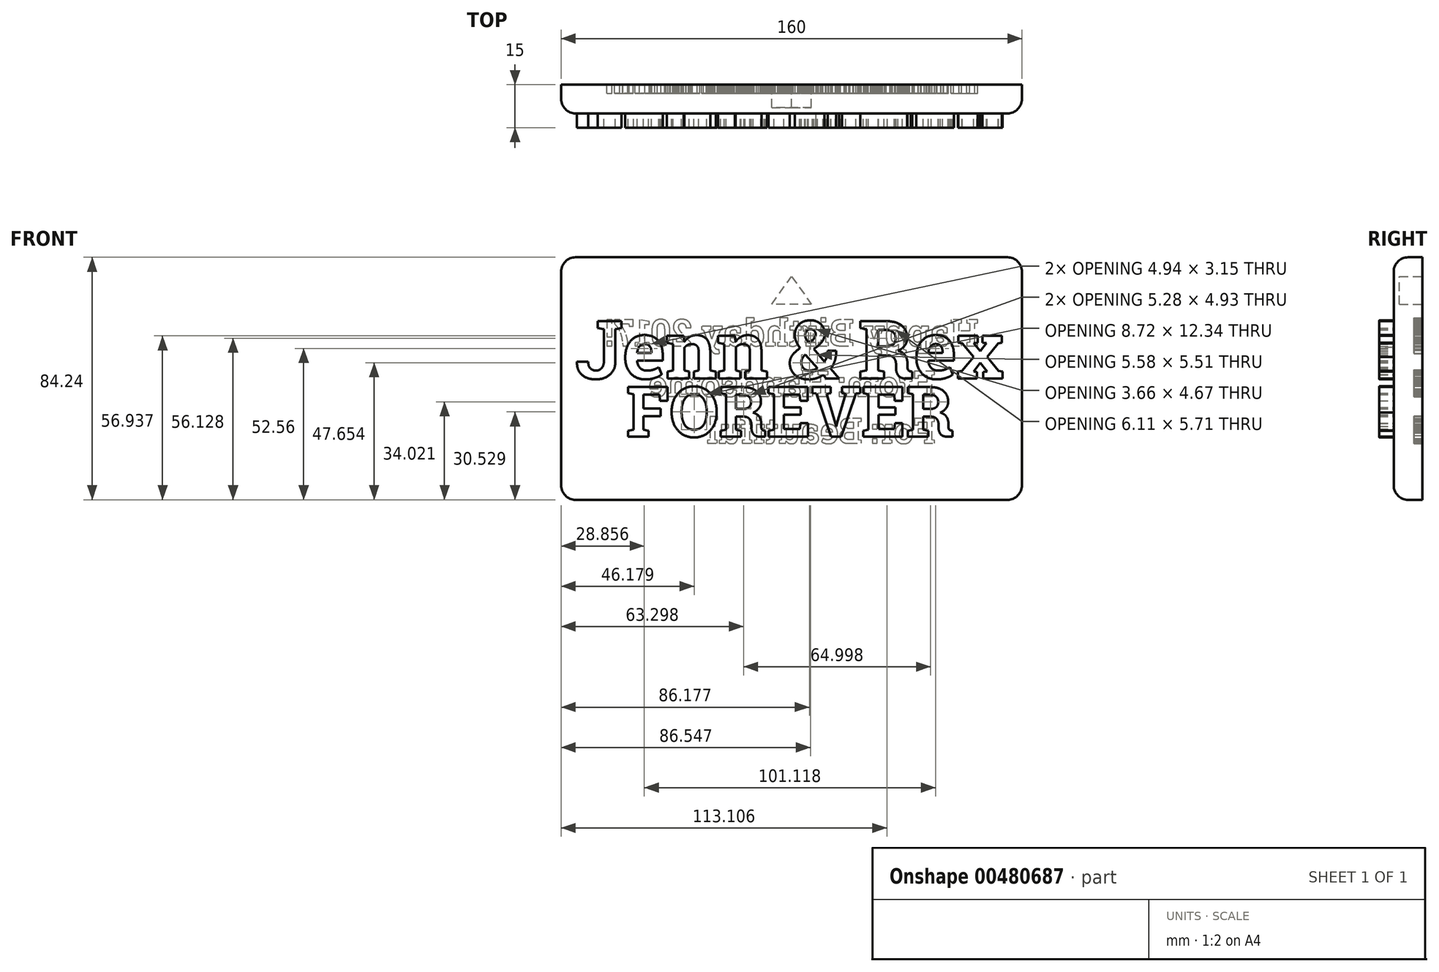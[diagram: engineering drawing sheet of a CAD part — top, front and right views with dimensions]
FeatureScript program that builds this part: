
annotation { "Feature Type Name" : "Feature", "Feature Type Description" : "" }
export const myFeature = defineFeature(function(context is Context, id is Id, definition is map)
    precondition{}
    {
        {
            var Q0;
            Q0=qCreatedBy(makeId("Front.planeOp"),FACE);
            var sketch = newSketch(context, id + "F0", { "sketchPlane" : qUnion([Q0])});
            skLineSegment(sketch, "E0.bottom", {"start": v(-80, 42.12) * mm, "end": v(80, 42.12) * mm});
            skLineSegment(sketch, "E0.top", {"start": v(-80, -42.12) * mm, "end": v(80, -42.12) * mm});
            skLineSegment(sketch, "E0.left", {"start": v(-80, 42.12) * mm, "end": v(-80, -42.12) * mm});
            skLineSegment(sketch, "E0.right", {"start": v(80, 42.12) * mm, "end": v(80, -42.12) * mm});
            skText(sketch, "E1", { "text": "Jenn & Rex", "fontName": "RobotoSlab-Bold.ttf"});
            skText(sketch, "E2", { "text": "FOREVER", "fontName": "RobotoSlab-Bold.ttf"});
            const initialGuessF0  = {"E1": [-0.075, 0, 1, 0, 0.0202], "E2": [-0.0574, -0.0202, 1, 0, 0.01745]};
            skSetInitialGuess(sketch, initialGuessF0);
            skSolve(sketch);
        }
        {
            var Q0;
            Q0=makeQuery(id+"F0.imprint","IMPRINT",FACE,{"disambiguationData":[TD([[makeQuery(id+"F0.imprint","IMPRINT",EDGE,{"derivedFrom":sQuery(id+"F0.wireOp",EDGE,"E1.sketch_text.stroke-0")}),-1.0]])]});
            var Q1;
            Q1=makeQuery(id+"F0.imprint","IMPRINT",FACE,{"disambiguationData":[TD([[makeQuery(id+"F0.imprint","IMPRINT",EDGE,{"derivedFrom":sQuery(id+"F0.wireOp",EDGE,"E1.sketch_text.stroke-18")}),-1.0]])]});
            var Q2;
            Q2=makeQuery(id+"F0.imprint","IMPRINT",FACE,{"disambiguationData":[TD([[makeQuery(id+"F0.imprint","IMPRINT",EDGE,{"derivedFrom":sQuery(id+"F0.wireOp",EDGE,"E1.sketch_text.stroke-42")}),-1.0]])]});
            var Q3;
            Q3=makeQuery(id+"F0.imprint","IMPRINT",FACE,{"disambiguationData":[TD([[makeQuery(id+"F0.imprint","IMPRINT",EDGE,{"derivedFrom":sQuery(id+"F0.wireOp",EDGE,"E1.sketch_text.stroke-68")}),-1.0]])]});
            var Q4;
            Q4=makeQuery(id+"F0.imprint","IMPRINT",FACE,{"disambiguationData":[TD([[makeQuery(id+"F0.imprint","IMPRINT",EDGE,{"derivedFrom":sQuery(id+"F0.wireOp",EDGE,"E1.sketch_text.stroke-94")}),-1.0]])]});
            var Q5;
            Q5=makeQuery(id+"F0.imprint","IMPRINT",FACE,{"disambiguationData":[TD([[makeQuery(id+"F0.imprint","IMPRINT",EDGE,{"derivedFrom":sQuery(id+"F0.wireOp",EDGE,"E1.sketch_text.stroke-136")}),-1.0]])]});
            var Q6;
            Q6=makeQuery(id+"F0.imprint","IMPRINT",FACE,{"disambiguationData":[TD([[makeQuery(id+"F0.imprint","IMPRINT",EDGE,{"derivedFrom":sQuery(id+"F0.wireOp",EDGE,"E2.sketch_text.stroke-95")}),-1.0]])]});
            var Q7;
            Q7=makeQuery(id+"F0.imprint","IMPRINT",FACE,{"disambiguationData":[TD([[makeQuery(id+"F0.imprint","IMPRINT",EDGE,{"derivedFrom":sQuery(id+"F0.wireOp",EDGE,"E2.sketch_text.stroke-74")}),-1.0]])]});
            var Q8;
            Q8=makeQuery(id+"F0.imprint","IMPRINT",FACE,{"disambiguationData":[TD([[makeQuery(id+"F0.imprint","IMPRINT",EDGE,{"derivedFrom":sQuery(id+"F0.wireOp",EDGE,"E2.sketch_text.stroke-38")}),-1.0]])]});
            var Q9;
            Q9=makeQuery(id+"F0.imprint","IMPRINT",FACE,{"disambiguationData":[TD([[makeQuery(id+"F0.imprint","IMPRINT",EDGE,{"derivedFrom":sQuery(id+"F0.wireOp",EDGE,"E2.sketch_text.stroke-18")}),-1.0]])]});
            var Q10;
            Q10=makeQuery(id+"F0.imprint","IMPRINT",FACE,{"disambiguationData":[TD([[makeQuery(id+"F0.imprint","IMPRINT",EDGE,{"derivedFrom":sQuery(id+"F0.wireOp",EDGE,"E2.sketch_text.stroke-0")}),-1.0]])]});
            var Q11;
            Q11=makeQuery(id+"F0.imprint","IMPRINT",FACE,{"disambiguationData":[TD([[makeQuery(id+"F0.imprint","IMPRINT",EDGE,{"derivedFrom":sQuery(id+"F0.wireOp",EDGE,"E1.sketch_text.stroke-172")}),-1.0]])]});
            var Q12;
            Q12=makeQuery(id+"F0.imprint","IMPRINT",FACE,{"disambiguationData":[TD([[makeQuery(id+"F0.imprint","IMPRINT",EDGE,{"derivedFrom":sQuery(id+"F0.wireOp",EDGE,"E1.sketch_text.stroke-196")}),-1.0]])]});
            var Q13;
            Q13=makeQuery(id+"F0.imprint","IMPRINT",FACE,{"disambiguationData":[TD([[makeQuery(id+"F0.imprint","IMPRINT",EDGE,{"derivedFrom":sQuery(id+"F0.wireOp",EDGE,"E2.sketch_text.stroke-134")}),-1.0]])]});
            var Q14;
            Q14=makeQuery(id+"F0.imprint","IMPRINT",FACE,{"disambiguationData":[TD([[makeQuery(id+"F0.imprint","IMPRINT",EDGE,{"derivedFrom":sQuery(id+"F0.wireOp",EDGE,"E2.sketch_text.stroke-113")}),-1.0]])]});
            extrude(context, id + "F1", {"entities" : qUnion([Q0, Q1, Q2, Q3, Q4, Q5, Q6, Q7, Q8, Q9, Q10, Q11, Q12, Q13, Q14]), "depth" : 5 * mm});
        }
        {
            var Q0;
            Q0=makeQuery(id+"F0.imprint","IMPRINT",FACE,{"disambiguationData":[TD([[makeQuery(id+"F0.imprint","IMPRINT",EDGE,{"derivedFrom":sQuery(id+"F0.wireOp",EDGE,"E0.bottom")}),-1.0]])]});
            var Q1;
            Q1=makeQuery(id+"F0.imprint","IMPRINT",FACE,{"disambiguationData":[TD([[makeQuery(id+"F0.imprint","IMPRINT",EDGE,{"derivedFrom":sQuery(id+"F0.wireOp",EDGE,"E1.sketch_text.stroke-165")}),1.0]])]});
            var Q2;
            Q2=makeQuery(id+"F0.imprint","IMPRINT",FACE,{"disambiguationData":[TD([[makeQuery(id+"F0.imprint","IMPRINT",EDGE,{"derivedFrom":sQuery(id+"F0.wireOp",EDGE,"E1.sketch_text.stroke-189")}),1.0]])]});
            var Q3;
            Q3=makeQuery(id+"F0.imprint","IMPRINT",FACE,{"disambiguationData":[TD([[makeQuery(id+"F0.imprint","IMPRINT",EDGE,{"derivedFrom":sQuery(id+"F0.wireOp",EDGE,"E1.sketch_text.stroke-119")}),1.0]])]});
            var Q4;
            Q4=makeQuery(id+"F0.imprint","IMPRINT",FACE,{"disambiguationData":[TD([[makeQuery(id+"F0.imprint","IMPRINT",EDGE,{"derivedFrom":sQuery(id+"F0.wireOp",EDGE,"E1.sketch_text.stroke-127")}),1.0]])]});
            var Q5;
            Q5=makeQuery(id+"F0.imprint","IMPRINT",FACE,{"disambiguationData":[TD([[makeQuery(id+"F0.imprint","IMPRINT",EDGE,{"derivedFrom":sQuery(id+"F0.wireOp",EDGE,"E2.sketch_text.stroke-163")}),1.0]])]});
            var Q6;
            Q6=makeQuery(id+"F0.imprint","IMPRINT",FACE,{"disambiguationData":[TD([[makeQuery(id+"F0.imprint","IMPRINT",EDGE,{"derivedFrom":sQuery(id+"F0.wireOp",EDGE,"E2.sketch_text.stroke-67")}),1.0]])]});
            var Q7;
            Q7=makeQuery(id+"F0.imprint","IMPRINT",FACE,{"disambiguationData":[TD([[makeQuery(id+"F0.imprint","IMPRINT",EDGE,{"derivedFrom":sQuery(id+"F0.wireOp",EDGE,"E2.sketch_text.stroke-28")}),1.0]])]});
            var Q8;
            Q8=makeQuery(id+"F0.imprint","IMPRINT",FACE,{"disambiguationData":[TD([[makeQuery(id+"F0.imprint","IMPRINT",EDGE,{"derivedFrom":sQuery(id+"F0.wireOp",EDGE,"E1.sketch_text.stroke-35")}),1.0]])]});
            var Q9;
            Q9=makeQuery(id+"F0.imprint","IMPRINT",FACE,{"disambiguationData":[TD([[makeQuery(id+"F0.imprint","IMPRINT",EDGE,{"derivedFrom":sQuery(id+"F0.wireOp",EDGE,"E1.sketch_text.stroke-18")}),-1.0]])]});
            var Q10;
            Q10=makeQuery(id+"F0.imprint","IMPRINT",FACE,{"disambiguationData":[TD([[makeQuery(id+"F0.imprint","IMPRINT",EDGE,{"derivedFrom":sQuery(id+"F0.wireOp",EDGE,"E1.sketch_text.stroke-0")}),-1.0]])]});
            var Q11;
            Q11=makeQuery(id+"F0.imprint","IMPRINT",FACE,{"disambiguationData":[TD([[makeQuery(id+"F0.imprint","IMPRINT",EDGE,{"derivedFrom":sQuery(id+"F0.wireOp",EDGE,"E1.sketch_text.stroke-42")}),-1.0]])]});
            var Q12;
            Q12=makeQuery(id+"F0.imprint","IMPRINT",FACE,{"disambiguationData":[TD([[makeQuery(id+"F0.imprint","IMPRINT",EDGE,{"derivedFrom":sQuery(id+"F0.wireOp",EDGE,"E1.sketch_text.stroke-68")}),-1.0]])]});
            var Q13;
            Q13=makeQuery(id+"F0.imprint","IMPRINT",FACE,{"disambiguationData":[TD([[makeQuery(id+"F0.imprint","IMPRINT",EDGE,{"derivedFrom":sQuery(id+"F0.wireOp",EDGE,"E1.sketch_text.stroke-94")}),-1.0]])]});
            var Q14;
            Q14=makeQuery(id+"F0.imprint","IMPRINT",FACE,{"disambiguationData":[TD([[makeQuery(id+"F0.imprint","IMPRINT",EDGE,{"derivedFrom":sQuery(id+"F0.wireOp",EDGE,"E1.sketch_text.stroke-136")}),-1.0]])]});
            var Q15;
            Q15=makeQuery(id+"F0.imprint","IMPRINT",FACE,{"disambiguationData":[TD([[makeQuery(id+"F0.imprint","IMPRINT",EDGE,{"derivedFrom":sQuery(id+"F0.wireOp",EDGE,"E1.sketch_text.stroke-172")}),-1.0]])]});
            var Q16;
            Q16=makeQuery(id+"F0.imprint","IMPRINT",FACE,{"disambiguationData":[TD([[makeQuery(id+"F0.imprint","IMPRINT",EDGE,{"derivedFrom":sQuery(id+"F0.wireOp",EDGE,"E1.sketch_text.stroke-196")}),-1.0]])]});
            var Q17;
            Q17=makeQuery(id+"F0.imprint","IMPRINT",FACE,{"disambiguationData":[TD([[makeQuery(id+"F0.imprint","IMPRINT",EDGE,{"derivedFrom":sQuery(id+"F0.wireOp",EDGE,"E2.sketch_text.stroke-134")}),-1.0]])]});
            var Q18;
            Q18=makeQuery(id+"F0.imprint","IMPRINT",FACE,{"disambiguationData":[TD([[makeQuery(id+"F0.imprint","IMPRINT",EDGE,{"derivedFrom":sQuery(id+"F0.wireOp",EDGE,"E2.sketch_text.stroke-113")}),-1.0]])]});
            var Q19;
            Q19=makeQuery(id+"F0.imprint","IMPRINT",FACE,{"disambiguationData":[TD([[makeQuery(id+"F0.imprint","IMPRINT",EDGE,{"derivedFrom":sQuery(id+"F0.wireOp",EDGE,"E2.sketch_text.stroke-95")}),-1.0]])]});
            var Q20;
            Q20=makeQuery(id+"F0.imprint","IMPRINT",FACE,{"disambiguationData":[TD([[makeQuery(id+"F0.imprint","IMPRINT",EDGE,{"derivedFrom":sQuery(id+"F0.wireOp",EDGE,"E2.sketch_text.stroke-74")}),-1.0]])]});
            var Q21;
            Q21=makeQuery(id+"F0.imprint","IMPRINT",FACE,{"disambiguationData":[TD([[makeQuery(id+"F0.imprint","IMPRINT",EDGE,{"derivedFrom":sQuery(id+"F0.wireOp",EDGE,"E2.sketch_text.stroke-38")}),-1.0]])]});
            var Q22;
            Q22=makeQuery(id+"F0.imprint","IMPRINT",FACE,{"disambiguationData":[TD([[makeQuery(id+"F0.imprint","IMPRINT",EDGE,{"derivedFrom":sQuery(id+"F0.wireOp",EDGE,"E2.sketch_text.stroke-18")}),-1.0]])]});
            var Q23;
            Q23=makeQuery(id+"F0.imprint","IMPRINT",FACE,{"disambiguationData":[TD([[makeQuery(id+"F0.imprint","IMPRINT",EDGE,{"derivedFrom":sQuery(id+"F0.wireOp",EDGE,"E2.sketch_text.stroke-0")}),-1.0]])]});
            extrude(context, id + "F2", {"entities" : qUnion([Q0, Q1, Q2, Q3, Q4, Q5, Q6, Q7, Q8, Q9, Q10, Q11, Q12, Q13, Q14, Q15, Q16, Q17, Q18, Q19, Q20, Q21, Q22, Q23]), "oppositeDirection" : true, "depth" : 10 * mm});
        }
        {
            var Q0;
            Q0=makeQuery(id+"F2.opExtrude","CAP_FACE",FACE,{"disambiguationData":[OSD([sQuery(id+"F0.wireOp",EDGE,"E0.bottom"),sQuery(id+"F0.wireOp",EDGE,"E0.top"),sQuery(id+"F0.wireOp",EDGE,"E0.left"),sQuery(id+"F0.wireOp",EDGE,"E0.right")])],"isStart":false});
            var sketch = newSketch(context, id + "F3", { "sketchPlane" : qUnion([Q0])});
            skText(sketch, "E3", { "text": "Happy Birthday 2017!\n", "fontName": "RobotoSlab-Bold.ttf"});
            skText(sketch, "E4", { "text": "From: Handsome\nFor: Beautiful", "fontName": "RobotoSlab-Bold.ttf"});
            skLineSegment(sketch, "E5", {"start": v(0, 35.5) * mm, "end": v(-6.9, 25.8) * mm});
            skLineSegment(sketch, "E6", {"start": v(-6.9, 25.8) * mm, "end": v(6.9, 25.8) * mm});
            skLineSegment(sketch, "E7", {"start": v(6.9, 25.8) * mm, "end": v(0, 35.5) * mm});
            const initialGuessF3  = {"E3": [-0.065, 0.01135, 1, 0, 0.00923], "E4": [-0.05, -0.00627, 1, 0, 0.00887]};
            skSetInitialGuess(sketch, initialGuessF3);
            skSolve(sketch);
        }
        {
            var Q0;
            Q0 = qSketchRegion(id + "F3", true);
            extrude(context, id + "F4", {"entities" : qUnion([Q0]), "operationType" : NewBodyOperationType.REMOVE, "oppositeDirection" : true, "depth" : 3 * mm});
        }
        {
            var Q0;
            Q0=makeQuery(id+"F3.imprint","IMPRINT",FACE,{"disambiguationData":[TD([[makeQuery(id+"F3.imprint","IMPRINT",EDGE,{"derivedFrom":sQuery(id+"F3.wireOp",EDGE,"E5")}),1.0]])]});
            extrude(context, id + "F5", {"entities" : qUnion([Q0]), "operationType" : NewBodyOperationType.REMOVE, "oppositeDirection" : true, "depth" : 8 * mm});
        }
        {
            var Q0;
            Q0=makeQuery(id+"F2.opExtrude","CAP_EDGE",EDGE,{"disambiguationData":[OSD([sQuery(id+"F0.wireOp",EDGE,"E0.left")])],"isStart":true});
            var Q1;
            Q1=makeQuery(id+"F2.opExtrude","CAP_EDGE",EDGE,{"disambiguationData":[OSD([sQuery(id+"F0.wireOp",EDGE,"E0.top")])],"isStart":true});
            var Q2;
            Q2=makeQuery(id+"F2.opExtrude","SWEPT_EDGE",EDGE,{"disambiguationData":[OSD([sQuery(id+"F0.wireOp",EDGE,"E0.top"),sQuery(id+"F0.wireOp",EDGE,"E0.left")])]});
            var Q3;
            Q3=makeQuery(id+"F2.opExtrude","CAP_EDGE",EDGE,{"disambiguationData":[OSD([sQuery(id+"F0.wireOp",EDGE,"E0.right")])],"isStart":true});
            var Q4;
            Q4=makeQuery(id+"F2.opExtrude","SWEPT_EDGE",EDGE,{"disambiguationData":[OSD([sQuery(id+"F0.wireOp",EDGE,"E0.top"),sQuery(id+"F0.wireOp",EDGE,"E0.right")])]});
            var Q5;
            Q5=makeQuery(id+"F2.opExtrude","CAP_EDGE",EDGE,{"disambiguationData":[OSD([sQuery(id+"F0.wireOp",EDGE,"E0.bottom")])],"isStart":true});
            var Q6;
            Q6=makeQuery(id+"F2.opExtrude","SWEPT_EDGE",EDGE,{"disambiguationData":[OSD([sQuery(id+"F0.wireOp",EDGE,"E0.bottom"),sQuery(id+"F0.wireOp",EDGE,"E0.right")])]});
            var Q7;
            Q7=makeQuery(id+"F2.opExtrude","SWEPT_EDGE",EDGE,{"disambiguationData":[OSD([sQuery(id+"F0.wireOp",EDGE,"E0.bottom"),sQuery(id+"F0.wireOp",EDGE,"E0.left")])]});
            fillet(context, id + "F6", {"entities" : qUnion([Q0, Q1, Q2, Q3, Q4, Q5, Q6, Q7]), "radius" : 5 * mm, "tangentPropagation" : true, "allowEdgeOverflow" : false});
        }
    });
